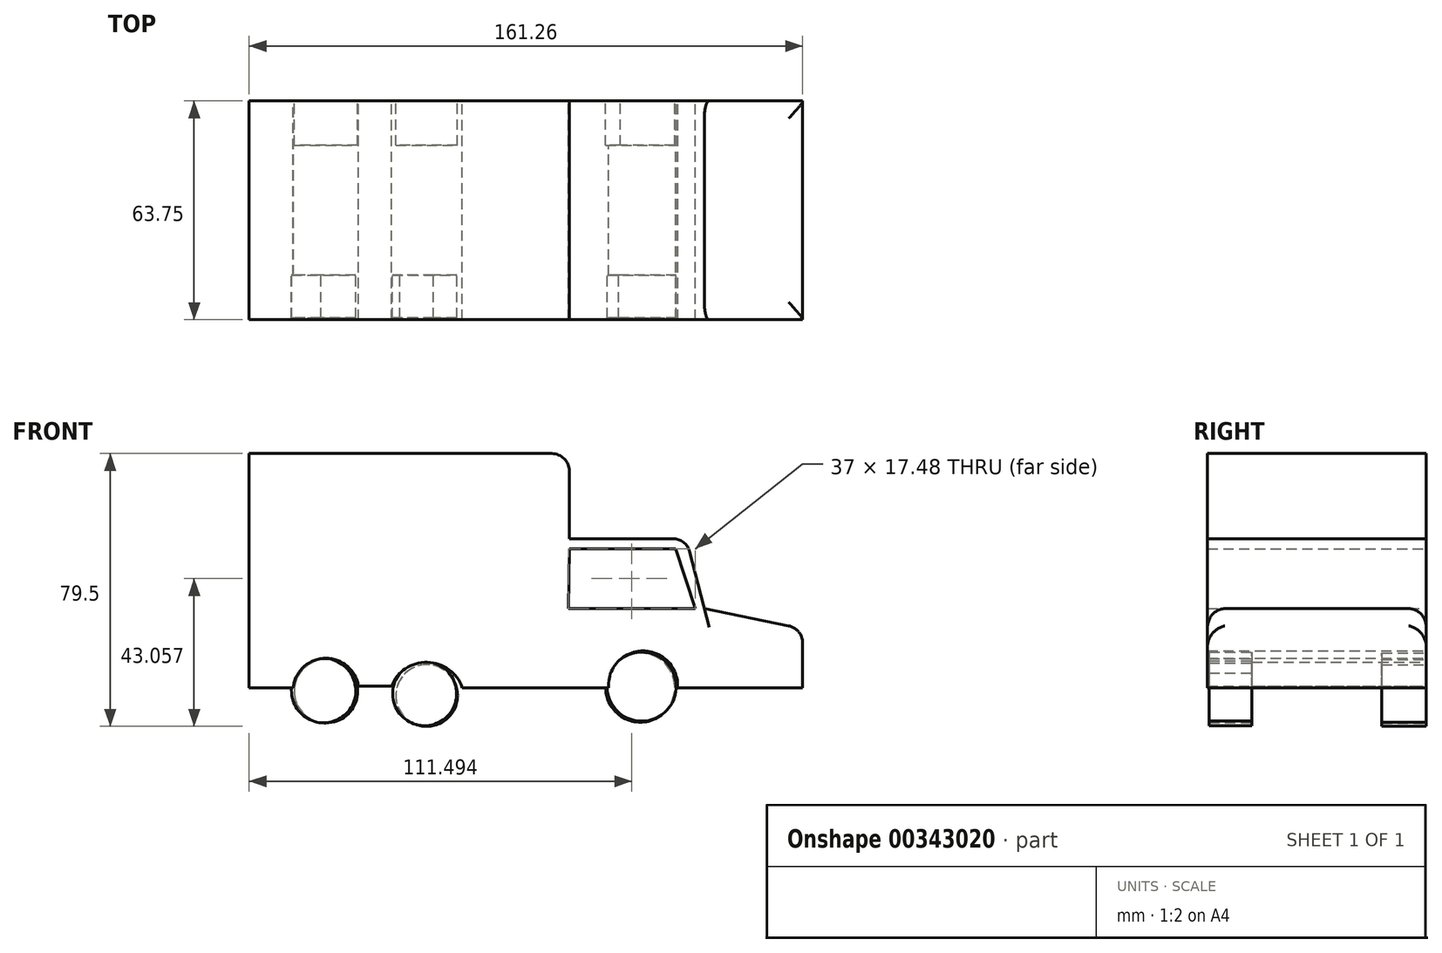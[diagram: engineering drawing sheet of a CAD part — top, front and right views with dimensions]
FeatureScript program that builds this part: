
annotation { "Feature Type Name" : "Feature", "Feature Type Description" : "" }
export const myFeature = defineFeature(function(context is Context, id is Id, definition is map)
    precondition{}
    {
        {
            var Q0;
            Q0=qCreatedBy(makeId("Front.planeOp"),FACE);
            var sketch = newSketch(context, id + "F0", { "sketchPlane" : qUnion([Q0])});
            skLineSegment(sketch, "E0", {"start": v(-62.08, 61.65) * mm, "end": v(-62.08, -6.56) * mm});
            skLineSegment(sketch, "E1", {"start": v(-62.08, -6.56) * mm, "end": v(-49.26, -6.56) * mm});
            skLineSegment(sketch, "E2", {"start": v(0, -6.56) * mm, "end": v(30.6, -6.56) * mm});
            skLineSegment(sketch, "E3", {"start": v(70.54, 16.47) * mm, "end": v(65.3, 36.87) * mm});
            skLineSegment(sketch, "E4", {"start": v(65.3, 36.87) * mm, "end": v(31.19, 36.87) * mm});
            skLineSegment(sketch, "E5", {"start": v(31.19, 36.87) * mm, "end": v(31.19, 61.65) * mm});
            skLineSegment(sketch, "E6", {"start": v(-62.08, 61.65) * mm, "end": v(31.19, 61.65) * mm});
            skArc(sketch, "E7.trimOffspring", {"start": v(-49.22, -6.12) * mm, "mid": v(-49.28, -6.34) * mm, "end": v(-49.33, -6.56) * mm});
            skPoint(sketch, "E8.start.orphan", {"position": v(51.88, -6.56) * mm});
            skLineSegment(sketch, "E9", {"start": v(30.6, -6.56) * mm, "end": v(42.64, -6.56) * mm});
            skArc(sketch, "E10", {"start": v(62.75, -6.56) * mm, "mid": v(52.7, 4.16) * mm, "end": v(42.64, -6.56) * mm});
            skLineSegment(sketch, "E11", {"start": v(62.75, -6.56) * mm, "end": v(99.18, -6.56) * mm});
            skLineSegment(sketch, "E12", {"start": v(99.18, -6.56) * mm, "end": v(99.18, 10.64) * mm});
            skLineSegment(sketch, "E13", {"start": v(99.18, 10.64) * mm, "end": v(70.54, 16.47) * mm});
            skArc(sketch, "E14", {"start": v(-30.23, -6.12) * mm, "mid": v(-39.73, 2.01) * mm, "end": v(-49.22, -6.12) * mm});
            skLineSegment(sketch, "E15", {"start": v(-30.23, -6.12) * mm, "end": v(-20.61, -6.12) * mm});
            skCircle(sketch, "E16", {"center": v(-39.73, -7.6) * mm, "radius": 9.26 * mm});
            skCircle(sketch, "E17", {"center": v(51.88, -6.56) * mm, "radius": 10.08 * mm});
            skCircle(sketch, "E18", {"center": v(-10.36, -8.85) * mm, "radius": 9 * mm});
            skArc(sketch, "E19", {"start": v(0, -6.56) * mm, "mid": v(-10.15, 0.85) * mm, "end": v(-20.61, -6.12) * mm});
            skLineSegment(sketch, "E20", {"start": v(31.19, 36.87) * mm, "end": v(30.6, -6.56) * mm});
            skLineSegment(sketch, "E21", {"start": v(70.54, 16.47) * mm, "end": v(30.91, 16.47) * mm});
            skLineSegment(sketch, "E22", {"start": v(61.3, 36.87) * mm, "end": v(67.91, 16.47) * mm});
            skPoint(sketch, "E22.endSnap0", {"position": v(67.91, 26.67) * mm});
            skLineSegment(sketch, "E23", {"start": v(62.24, 33.95) * mm, "end": v(31.15, 33.95) * mm});
            skSolve(sketch);
        }
        {
            var Q0;
            {var subQ1=sQuery(id+"F0.wireOp",EDGE,"E0");Q0=makeQuery(id+"F0.imprint","IMPRINT",FACE,{"disambiguationData":[TD([[makeQuery(id+"F0.imprint","IMPRINT",EDGE,{"derivedFrom":subQ1}),1.0]])]});}
            var Q1;
            {var subQ0=sQuery(id+"F0.wireOp",EDGE,"E3");Q1=makeQuery(id+"F0.imprint","IMPRINT",FACE,{"disambiguationData":[TD([[makeQuery(id+"F0.imprint","IMPRINT",EDGE,{"derivedFrom":subQ0}),1.0]])]});}
            var Q2;
            {var subQ0=sQuery(id+"F0.wireOp",EDGE,"E10");var subQ1=sQuery(id+"F0.wireOp",EDGE,"E9");var subQ2=makeQuery(id+"F0.imprint","INTERSECT",VERTEX,{"derivedFrom":[subQ1,subQ0]});Q2=makeQuery(id+"F0.imprint","IMPRINT",FACE,{"disambiguationData":[TD([[makeQuery(id+"F0.imprint","IMPRINT",EDGE,{"disambiguationData":[TD([[subQ2,1.0]])],"derivedFrom":subQ1}),1.0]])]});}
            var Q3;
            {var subQ0=sQuery(id+"F0.wireOp",EDGE,"E11");Q3=makeQuery(id+"F0.imprint","IMPRINT",FACE,{"disambiguationData":[TD([[makeQuery(id+"F0.imprint","IMPRINT",EDGE,{"derivedFrom":subQ0}),1.0]])]});}
            var Q4;
            {var subQ5=sQuery(id+"F0.wireOp",EDGE,"E23");Q4=makeQuery(id+"F0.imprint","IMPRINT",FACE,{"disambiguationData":[TD([[makeQuery(id+"F0.imprint","IMPRINT",EDGE,{"derivedFrom":subQ5}),-1.0]])]});}
            extrude(context, id + "F1", {"entities" : qUnion([Q0, Q1, Q2, Q3, Q4]), "depth" : 63.5 * mm});
        }
        {
            var Q0;
            Q0 = qSketchRegion(id + "F0", true);
            extrude(context, id + "F2", {"entities" : qUnion([Q0]), "operationType" : NewBodyOperationType.ADD, "depth" : 12.7 * mm, "hasSecondDirection" : true, "secondDirectionOppositeDirection" : true, "secondDirectionDepth" : 0.25 * mm});
        }
        {
            var Q0;
            Q0=qCreatedBy(makeId("Front.planeOp"),FACE);
            var sketch = newSketch(context, id + "F3", { "sketchPlane" : qUnion([Q0])});
            skCircle(sketch, "E24", {"center": v(-40.4, -7.43) * mm, "radius": 9.37 * mm});
            skCircle(sketch, "E25", {"center": v(-10.95, -8.3) * mm, "radius": 9.33 * mm});
            skCircle(sketch, "E26", {"center": v(52.3, -6.27) * mm, "radius": 10.06 * mm});
            skSolve(sketch);
        }
        {
            var Q0;
            Q0 = qSketchRegion(id + "F3", true);
            extrude(context, id + "F4", {"entities" : qUnion([Q0]), "operationType" : NewBodyOperationType.ADD, "depth" : 63 * mm, "hasSecondDirection" : true, "secondDirectionOppositeDirection" : false, "secondDirectionDepth" : 50.55 * mm});
        }
        {
            var Q0;
            {var subQ0=sQuery(id+"F0.wireOp",EDGE,"E13");var subQ1=sQuery(id+"F0.wireOp",EDGE,"E12");Q0=makeQuery(id+"F2.boolean.opBoolean","MERGE",EDGE,{"derivedFrom":[makeQuery(id+"F1.opExtrude","SWEPT_EDGE",EDGE,{"disambiguationData":[OSD([subQ1,subQ0])]}),makeQuery(id+"F2.opExtrude","SWEPT_EDGE",EDGE,{"disambiguationData":[OSD([subQ1,subQ0])]})]});}
            var Q1;
            {var subQ0=sQuery(id+"F0.wireOp",EDGE,"E4");var subQ1=sQuery(id+"F0.wireOp",EDGE,"E3");Q1=makeQuery(id+"F2.boolean.opBoolean","MERGE",EDGE,{"derivedFrom":[makeQuery(id+"F1.opExtrude","SWEPT_EDGE",EDGE,{"disambiguationData":[OSD([subQ1,subQ0])]}),makeQuery(id+"F2.opExtrude","SWEPT_EDGE",EDGE,{"disambiguationData":[OSD([subQ1,subQ0])]})]});}
            var Q2;
            {var subQ0=sQuery(id+"F0.wireOp",EDGE,"E6");var subQ1=sQuery(id+"F0.wireOp",EDGE,"E5");Q2=makeQuery(id+"F2.boolean.opBoolean","MERGE",EDGE,{"derivedFrom":[makeQuery(id+"F1.opExtrude","SWEPT_EDGE",EDGE,{"disambiguationData":[OSD([subQ1,subQ0])]}),makeQuery(id+"F2.opExtrude","SWEPT_EDGE",EDGE,{"disambiguationData":[OSD([subQ1,subQ0])]})]});}
            var Q3;
            Q3=makeQuery(id+"F2.opExtrude","CAP_EDGE",EDGE,{"disambiguationData":[OSD([sQuery(id+"F0.wireOp",EDGE,"E13")])],"isStart":true});
            var Q4;
            Q4=makeQuery(id+"F1.opExtrude","CAP_EDGE",EDGE,{"disambiguationData":[OSD([sQuery(id+"F0.wireOp",EDGE,"E13")])],"isStart":false});
            fillet(context, id + "F5", {"entities" : qUnion([Q0, Q1, Q2, Q3, Q4]), "radius" : 5.08 * mm, "tangentPropagation" : true, "allowEdgeOverflow" : false});
        }
    });
